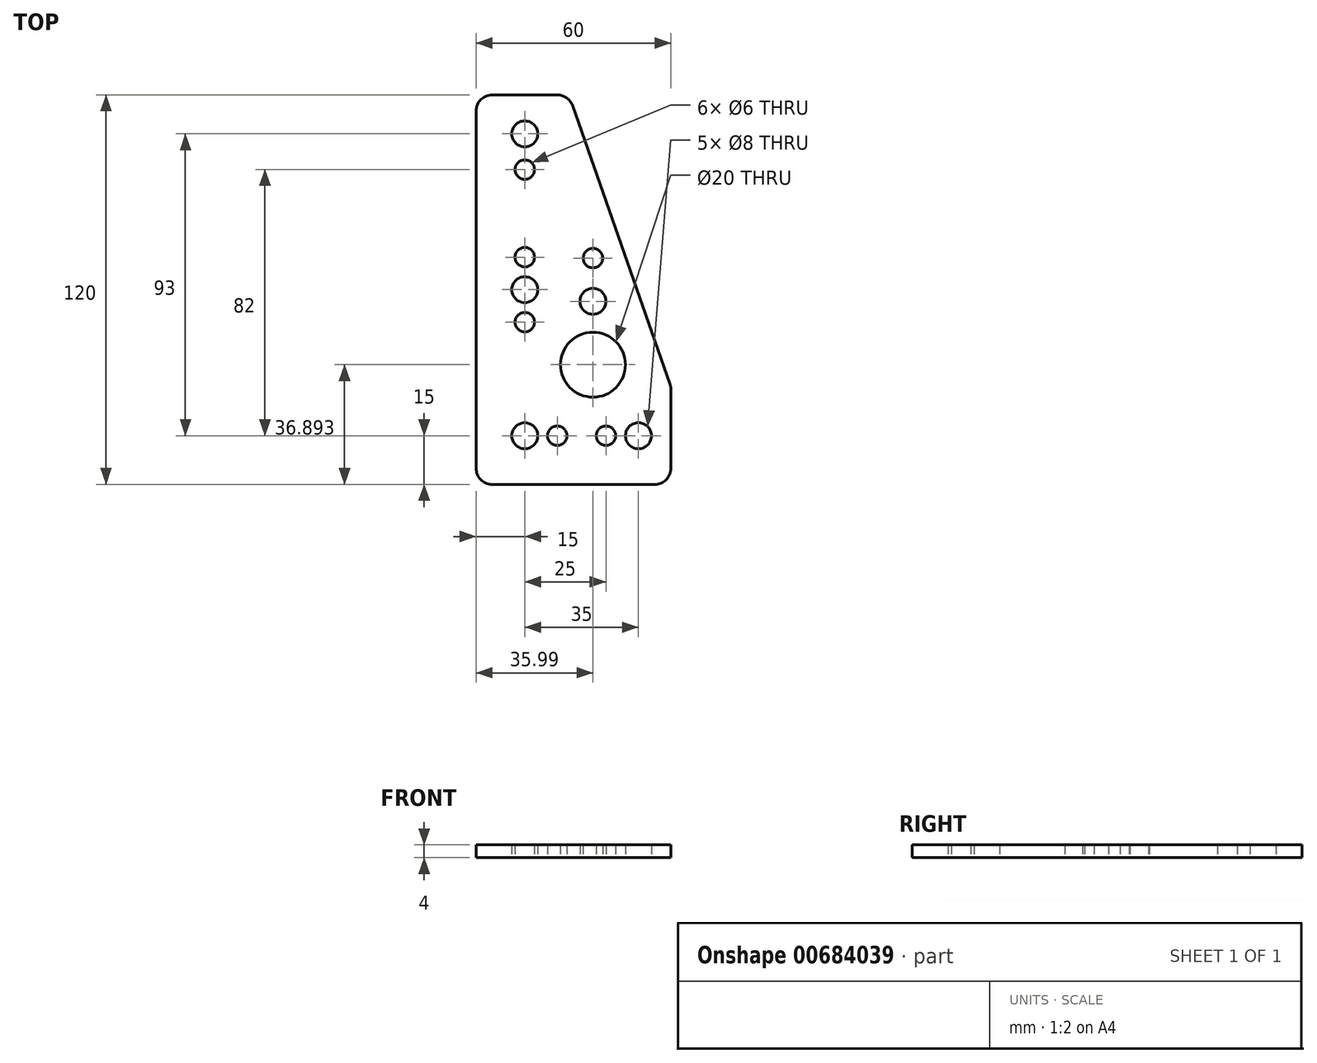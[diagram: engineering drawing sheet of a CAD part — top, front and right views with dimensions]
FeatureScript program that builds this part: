
annotation { "Feature Type Name" : "Feature", "Feature Type Description" : "" }
export const myFeature = defineFeature(function(context is Context, id is Id, definition is map)
    precondition{}
    {
        {
            var Q0;
            Q0=qCreatedBy(makeId("Top.planeOp"),FACE);
            var sketch = newSketch(context, id + "F0", { "sketchPlane" : qUnion([Q0])});
            skLineSegment(sketch, "E0", {"start": v(5, 0) * mm, "end": v(55, 0) * mm});
            skLineSegment(sketch, "E1", {"start": v(0, 115) * mm, "end": v(0, 5) * mm});
            skLineSegment(sketch, "E2", {"start": v(5, 120) * mm, "end": v(25, 120) * mm});
            skLineSegment(sketch, "E3", {"start": v(60, 29.19) * mm, "end": v(60, 5) * mm});
            skLineSegment(sketch, "E4", {"start": v(30, 120) * mm, "end": v(30, 39.92) * mm, "construction": true});
            skLineSegment(sketch, "E5", {"start": v(43.24, 30) * mm, "end": v(95.1, 30) * mm, "construction": true});
            skLineSegment(sketch, "E6", {"start": v(29.72, 116.65) * mm, "end": v(59.72, 30.84) * mm});
            skPoint(sketch, "E7.newPointB", {"position": v(0, 191.72) * mm});
            skArc(sketch, "E7.filletArc", {"start": v(5, 120) * mm, "mid": v(1.46, 118.54) * mm, "end": v(0, 115) * mm});
            skArc(sketch, "E8.filletArc", {"start": v(29.72, 116.65) * mm, "mid": v(27.9, 119.08) * mm, "end": v(25, 120) * mm});
            skArc(sketch, "E9.filletArc", {"start": v(60, 29.19) * mm, "mid": v(59.93, 30.03) * mm, "end": v(59.72, 30.84) * mm});
            skPoint(sketch, "E10.newPointA", {"position": v(73.75, 0) * mm});
            skArc(sketch, "E10.filletArc", {"start": v(55, 0) * mm, "mid": v(58.54, 1.46) * mm, "end": v(60, 5) * mm});
            skPoint(sketch, "E11.visualSharp", {"position": v(0, 0) * mm});
            skArc(sketch, "E11.filletArc", {"start": v(0, 5) * mm, "mid": v(1.46, 1.46) * mm, "end": v(5, 0) * mm});
            skCircle(sketch, "E12", {"center": v(15, 108) * mm, "radius": 4 * mm});
            skPoint(sketch, "E12.centerSnap0", {"position": v(15, 120) * mm});
            skCircle(sketch, "E13", {"center": v(15, 15) * mm, "radius": 4 * mm});
            skCircle(sketch, "E14", {"center": v(15, 60) * mm, "radius": 4 * mm});
            skCircle(sketch, "E15", {"center": v(50, 15) * mm, "radius": 4 * mm});
            skCircle(sketch, "E16", {"center": v(40, 15) * mm, "radius": 3 * mm});
            skCircle(sketch, "E17", {"center": v(15, 97) * mm, "radius": 3 * mm});
            skCircle(sketch, "E18", {"center": v(15, 70) * mm, "radius": 3 * mm});
            skCircle(sketch, "E19", {"center": v(15, 50) * mm, "radius": 3 * mm});
            skCircle(sketch, "E20", {"center": v(25, 15) * mm, "radius": 3 * mm});
            skCircle(sketch, "E21", {"center": v(36, 36.9) * mm, "radius": 10 * mm});
            skCircle(sketch, "E22", {"center": v(36, 56.42) * mm, "radius": 4 * mm});
            skCircle(sketch, "E23", {"center": v(36, 69.71) * mm, "radius": 3 * mm});
            skSolve(sketch);
        }
        {
            var Q0;
            Q0 = qSketchRegion(id + "F0", true);
            extrude(context, id + "F1", {"entities" : qUnion([Q0]), "depth" : 4 * mm, "offsetDistance" : 25 * mm});
        }
    });
